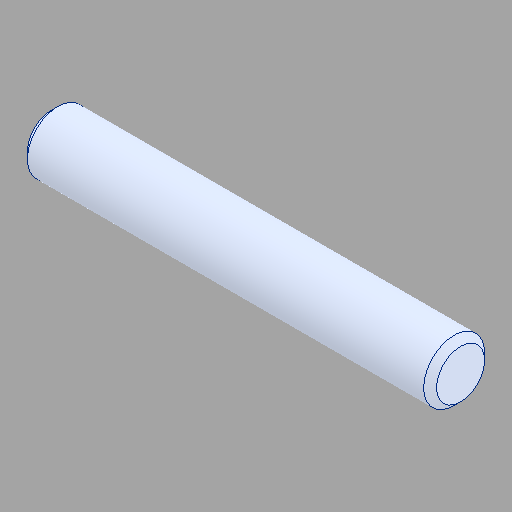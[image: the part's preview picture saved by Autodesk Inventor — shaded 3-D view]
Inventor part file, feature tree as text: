
AUTODESK INVENTOR PART (.ipt)
format: ipt  version: 2024.2 (Build 282272000, 272)  size: 93,696 bytes
history: native  units: in
note: dims shown in document units (in); Inventor stores cm internally (conversion verified against a paired STEP export)
features: chamfer x1
ambient origin geometry x8: Origin, YZ Plane, XZ Plane, XY Plane, X Axis, Y Axis, Z Axis, Center Point
bodies: Solid1 (feature_tree)
feature tree (1):
  chamfer  "Chamfer1"  [1 undecoded]
note: 1 required parameter value undecoded (feature->parameter linkage not recoverable at this tier; creation-order binding heuristic only, values carry confidence <= 0.55)
